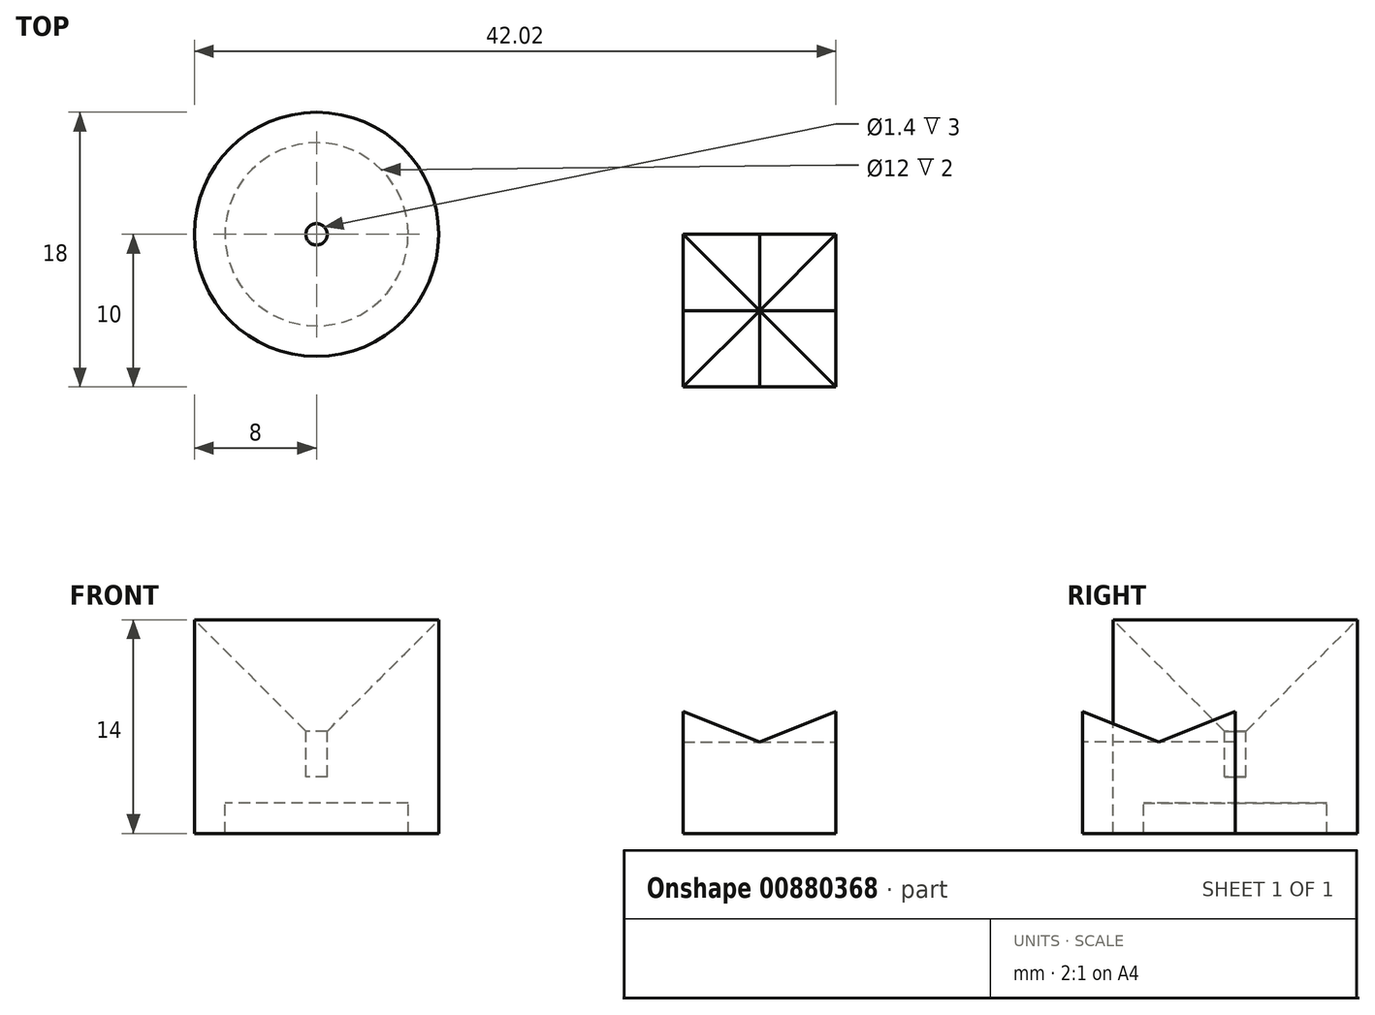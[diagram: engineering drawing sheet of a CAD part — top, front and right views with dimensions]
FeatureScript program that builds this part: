
annotation { "Feature Type Name" : "Feature", "Feature Type Description" : "" }
export const myFeature = defineFeature(function(context is Context, id is Id, definition is map)
    precondition{}
    {
        {
            var Q0;
            Q0=qCreatedBy(makeId("Front.planeOp"),FACE);
            var sketch = newSketch(context, id + "F0", { "sketchPlane" : qUnion([Q0])});
            skLineSegment(sketch, "E0", {"start": v(0, 2) * mm, "end": v(-6, 2) * mm});
            skLineSegment(sketch, "E1", {"start": v(-6, 2) * mm, "end": v(-6, 0) * mm});
            skLineSegment(sketch, "E2", {"start": v(-6, 0) * mm, "end": v(-8, 0) * mm});
            skLineSegment(sketch, "E3", {"start": v(-8, 0) * mm, "end": v(-8, 14) * mm});
            skLineSegment(sketch, "E4", {"start": v(-8, 14) * mm, "end": v(-0.7, 6.7) * mm});
            skLineSegment(sketch, "E5", {"start": v(0, 3.7) * mm, "end": v(0, 2) * mm});
            skLineSegment(sketch, "E6", {"start": v(0, 3.7) * mm, "end": v(-0.7, 3.7) * mm});
            skLineSegment(sketch, "E7", {"start": v(-0.7, 3.7) * mm, "end": v(-0.7, 6.7) * mm});
            skPoint(sketch, "E8.orphan", {"position": v(0, 6) * mm});
            skSolve(sketch);
        }
        {
            var Q0;
            Q0 = qSketchRegion(id + "F0", true);
            var Q1;
            Q1=sQuery(id+"F0.wireOp",EDGE,"E5");
            revolve(context, id + "F1", {"surfaceOperationType" : NewSurfaceOperationType.NEW, "entities" : qUnion([Q0]), "axis" : qUnion([Q1]), "revolveType" : RevolveType.FULL});
        }
        {
            var Q0;
            Q0=qCreatedBy(makeId("Top.planeOp"),FACE);
            var sketch = newSketch(context, id + "F2", { "sketchPlane" : qUnion([Q0])});
            skLineSegment(sketch, "E9.bottom", {"start": v(24.02, 0) * mm, "end": v(34.02, 0) * mm});
            skLineSegment(sketch, "E9.top", {"start": v(24.02, -10) * mm, "end": v(34.02, -10) * mm});
            skLineSegment(sketch, "E9.left", {"start": v(24.02, 0) * mm, "end": v(24.02, -10) * mm});
            skLineSegment(sketch, "E9.right", {"start": v(34.02, 0) * mm, "end": v(34.02, -10) * mm});
            skSolve(sketch);
        }
        {
            var Q0;
            Q0 = qSketchRegion(id + "F2", true);
            extrude(context, id + "F3", {"entities" : qUnion([Q0]), "depth" : 8 * mm, "offsetDistance" : 25 * mm});
        }
        {
            var Q0;
            Q0=makeQuery(id+"F3.opExtrude","SWEPT_FACE",FACE,{"disambiguationData":[OSD([sQuery(id+"F2.wireOp",EDGE,"E9.top")])]});
            var sketch = newSketch(context, id + "F4", { "sketchPlane" : qUnion([Q0])});
            skLineSegment(sketch, "E10", {"start": v(24.02, 8) * mm, "end": v(34.02, 8) * mm});
            skLineSegment(sketch, "E11", {"start": v(34.02, 8) * mm, "end": v(29.02, 6) * mm});
            skPoint(sketch, "E11.endSnap0", {"position": v(29.02, 8) * mm});
            skLineSegment(sketch, "E12", {"start": v(24.02, 8) * mm, "end": v(29.02, 6) * mm});
            skSolve(sketch);
        }
        {
            var Q0;
            Q0 = qSketchRegion(id + "F4", true);
            extrude(context, id + "F5", {"entities" : qUnion([Q0]), "operationType" : NewBodyOperationType.REMOVE, "endBound" : BoundingType.UP_TO_NEXT, "oppositeDirection" : true, "depth" : 25 * mm, "offsetDistance" : 25 * mm});
        }
        {
            var Q0;
            Q0=makeQuery(id+"F3.opExtrude","SWEPT_FACE",FACE,{"disambiguationData":[OSD([sQuery(id+"F2.wireOp",EDGE,"E9.right")])]});
            var sketch = newSketch(context, id + "F6", { "sketchPlane" : qUnion([Q0])});
            skLineSegment(sketch, "E13", {"start": v(-10, 8) * mm, "end": v(0, 8) * mm});
            skLineSegment(sketch, "E14", {"start": v(0, 8) * mm, "end": v(-5, 6) * mm});
            skPoint(sketch, "E14.endSnap0", {"position": v(-5, 8) * mm});
            skLineSegment(sketch, "E15", {"start": v(-10, 8) * mm, "end": v(-5, 6) * mm});
            skSolve(sketch);
        }
        {
            var Q0;
            Q0 = qSketchRegion(id + "F6", true);
            extrude(context, id + "F7", {"entities" : qUnion([Q0]), "operationType" : NewBodyOperationType.REMOVE, "oppositeDirection" : true, "depth" : 25 * mm, "offsetDistance" : 25 * mm});
        }
    });
